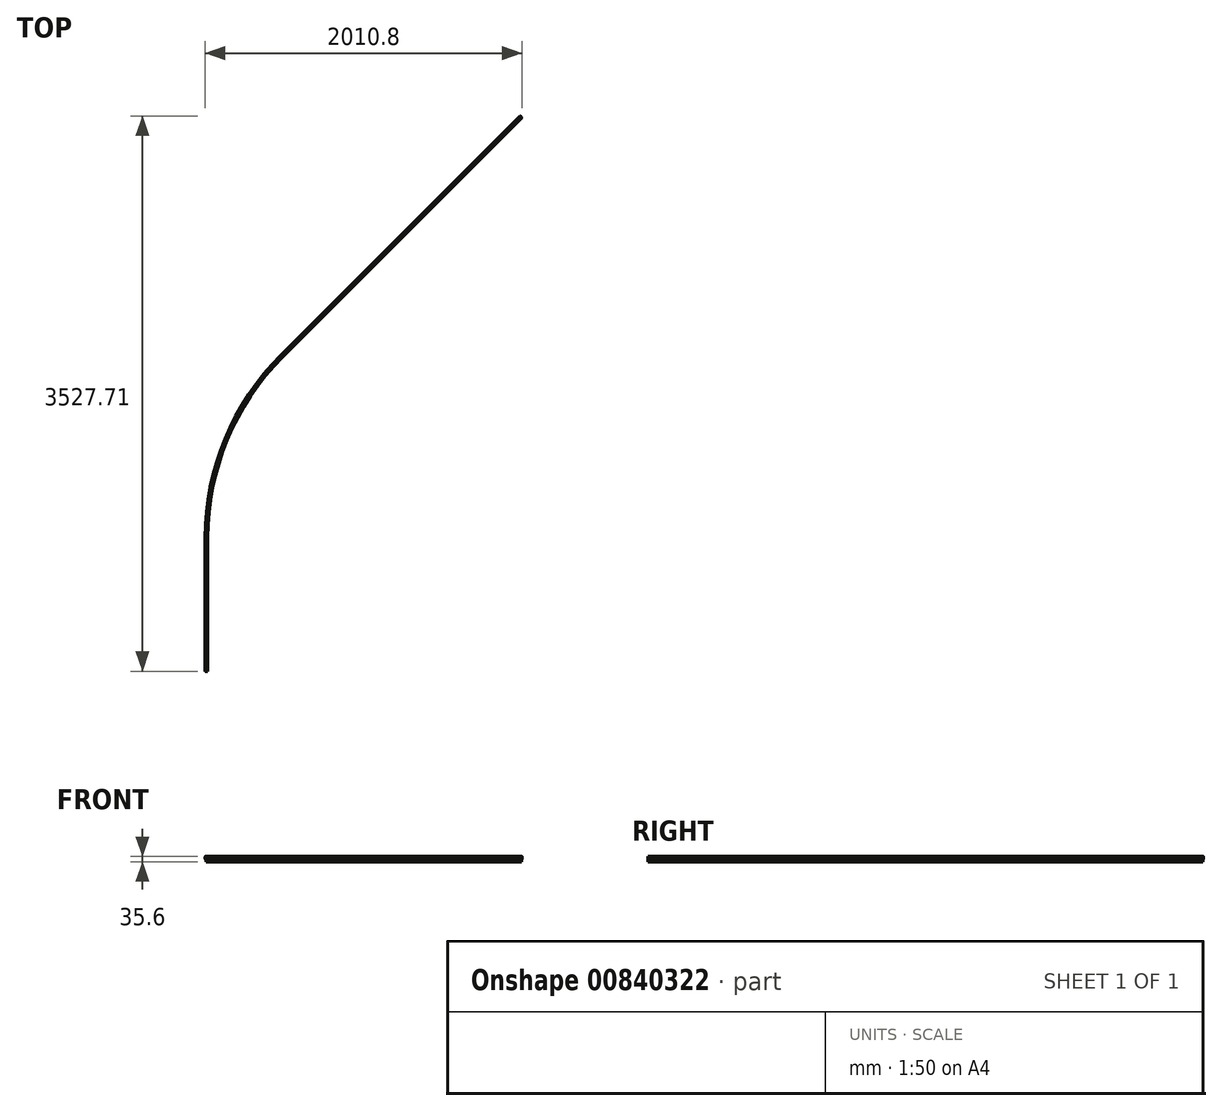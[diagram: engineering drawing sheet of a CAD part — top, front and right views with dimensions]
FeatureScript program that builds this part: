
annotation { "Feature Type Name" : "Feature", "Feature Type Description" : "" }
export const myFeature = defineFeature(function(context is Context, id is Id, definition is map)
    precondition{}
    {
        {
            var Q0;
            Q0=qCreatedBy(makeId("Top.planeOp"),FACE);
            var sketch = newSketch(context, id + "F0", { "sketchPlane" : qUnion([Q0])});
            skLineSegment(sketch, "E0", {"start": v(0, 0) * mm, "end": v(0, 850) * mm});
            skArc(sketch, "E1", {"start": v(476.4, 2000.1) * mm, "mid": v(123.8, 1472.43) * mm, "end": v(0, 850) * mm});
            skLineSegment(sketch, "E2", {"start": v(476.4, 2000.1) * mm, "end": v(1996.67, 3520.39) * mm});
            skLineSegment(sketch, "E3", {"start": v(0, 850) * mm, "end": v(1626.5, 850) * mm, "construction": true});
            skLineSegment(sketch, "E4", {"start": v(476.4, 2000.1) * mm, "end": v(1626.5, 850) * mm, "construction": true});
            skSolve(sketch);
        }
        {
            var Q0;
            Q0=qCreatedBy(makeId("Front.planeOp"),FACE);
            var sketch = newSketch(context, id + "F1", { "sketchPlane" : qUnion([Q0])});
            skLineSegment(sketch, "E5.bottom", {"start": v(0, 15) * mm, "end": v(-5, 15) * mm});
            skLineSegment(sketch, "E5.top", {"start": v(0, -15) * mm, "end": v(-5, -15) * mm});
            skLineSegment(sketch, "E5.left", {"start": v(0, 15) * mm, "end": v(0, -15) * mm});
            skLineSegment(sketch, "E5.right", {"start": v(-5, 15) * mm, "end": v(-5, -15) * mm});
            skSolve(sketch);
        }
        {
            var Q0;
            Q0=makeQuery(id+"F1.imprint","IMPRINT",FACE,{"disambiguationData":[TD([[makeQuery(id+"F1.imprint","IMPRINT",EDGE,{"derivedFrom":sQuery(id+"F1.wireOp",EDGE,"E5.bottom")}),1.0]])]});
            var Q1;
            Q1=sQuery(id+"F0.wireOp",EDGE,"E0");
            var Q2;
            Q2=sQuery(id+"F0.wireOp",EDGE,"E1");
            var Q3;
            Q3=sQuery(id+"F0.wireOp",EDGE,"E2");
            sweep(context, id + "F2", {"profiles" : qUnion([Q0]), "path" : qUnion([Q1, Q2, Q3])});
        }
        {
            var Q0;
            Q0=makeQuery(id+"F2.opSweep","CAP_FACE",FACE,{"disambiguationData":[OSD([sQuery(id+"F0.wireOp",VERTEX,"E0.start"),sQuery(id+"F1.wireOp",EDGE,"E5.bottom"),sQuery(id+"F1.wireOp",EDGE,"E5.top"),sQuery(id+"F1.wireOp",EDGE,"E5.left"),sQuery(id+"F1.wireOp",EDGE,"E5.right")])],"isStart":true});
            var sketch = newSketch(context, id + "F3", { "sketchPlane" : qUnion([Q0])});
            skLineSegment(sketch, "E6", {"start": v(-10.35, 2.8) * mm, "end": v(-10.35, 18.6) * mm});
            skLineSegment(sketch, "E7", {"start": v(-8.35, 20.6) * mm, "end": v(3.35, 20.6) * mm});
            skLineSegment(sketch, "E8", {"start": v(5.35, 18.6) * mm, "end": v(5.35, 2.8) * mm});
            skLineSegment(sketch, "E9", {"start": v(3.35, 0.8) * mm, "end": v(0.05, 0.8) * mm});
            skLineSegment(sketch, "E10", {"start": v(0.05, 0.8) * mm, "end": v(0.05, 15) * mm});
            skLineSegment(sketch, "E11", {"start": v(0.05, 15) * mm, "end": v(-5.05, 15) * mm});
            skLineSegment(sketch, "E12", {"start": v(-5.05, 15) * mm, "end": v(-5.05, 0.8) * mm});
            skLineSegment(sketch, "E13", {"start": v(-5.05, 0.8) * mm, "end": v(-8.35, 0.8) * mm});
            skPoint(sketch, "E14.visualSharp", {"position": v(-10.35, 20.6) * mm});
            skArc(sketch, "E14.filletArc", {"start": v(-8.35, 20.6) * mm, "mid": v(-9.76, 20.01) * mm, "end": v(-10.35, 18.6) * mm});
            skPoint(sketch, "E15.visualSharp", {"position": v(5.35, 20.6) * mm});
            skArc(sketch, "E15.filletArc", {"start": v(5.35, 18.6) * mm, "mid": v(4.76, 20.01) * mm, "end": v(3.35, 20.6) * mm});
            skPoint(sketch, "E16.visualSharp", {"position": v(5.35, 0.8) * mm});
            skArc(sketch, "E16.filletArc", {"start": v(3.35, 0.8) * mm, "mid": v(4.76, 1.39) * mm, "end": v(5.35, 2.8) * mm});
            skPoint(sketch, "E17.visualSharp", {"position": v(-10.35, 0.8) * mm});
            skArc(sketch, "E17.filletArc", {"start": v(-10.35, 2.8) * mm, "mid": v(-9.76, 1.39) * mm, "end": v(-8.35, 0.8) * mm});
            skSolve(sketch);
        }
        {
            var Q0;
            Q0=qSketchRegion(id+"F3",true);
            var Q1;
            Q1=makeQuery(id+"F2.opSweep","SWEPT_EDGE",EDGE,{"disambiguationData":[OSD([sQuery(id+"F0.wireOp",EDGE,"E0"),sQuery(id+"F1.wireOp",EDGE,"E5.bottom"),sQuery(id+"F1.wireOp",EDGE,"E5.left")])]});
            var Q2;
            Q2=makeQuery(id+"F2.opSweep","SWEPT_EDGE",EDGE,{"disambiguationData":[OSD([sQuery(id+"F0.wireOp",EDGE,"E1"),sQuery(id+"F1.wireOp",EDGE,"E5.bottom"),sQuery(id+"F1.wireOp",EDGE,"E5.left")])]});
            var Q3;
            Q3=makeQuery(id+"F2.opSweep","SWEPT_EDGE",EDGE,{"disambiguationData":[OSD([sQuery(id+"F0.wireOp",EDGE,"E2"),sQuery(id+"F1.wireOp",EDGE,"E5.bottom"),sQuery(id+"F1.wireOp",EDGE,"E5.left")])]});
            sweep(context, id + "F4", {"profiles" : qUnion([Q0]), "path" : qUnion([Q1, Q2, Q3])});
        }
    });
